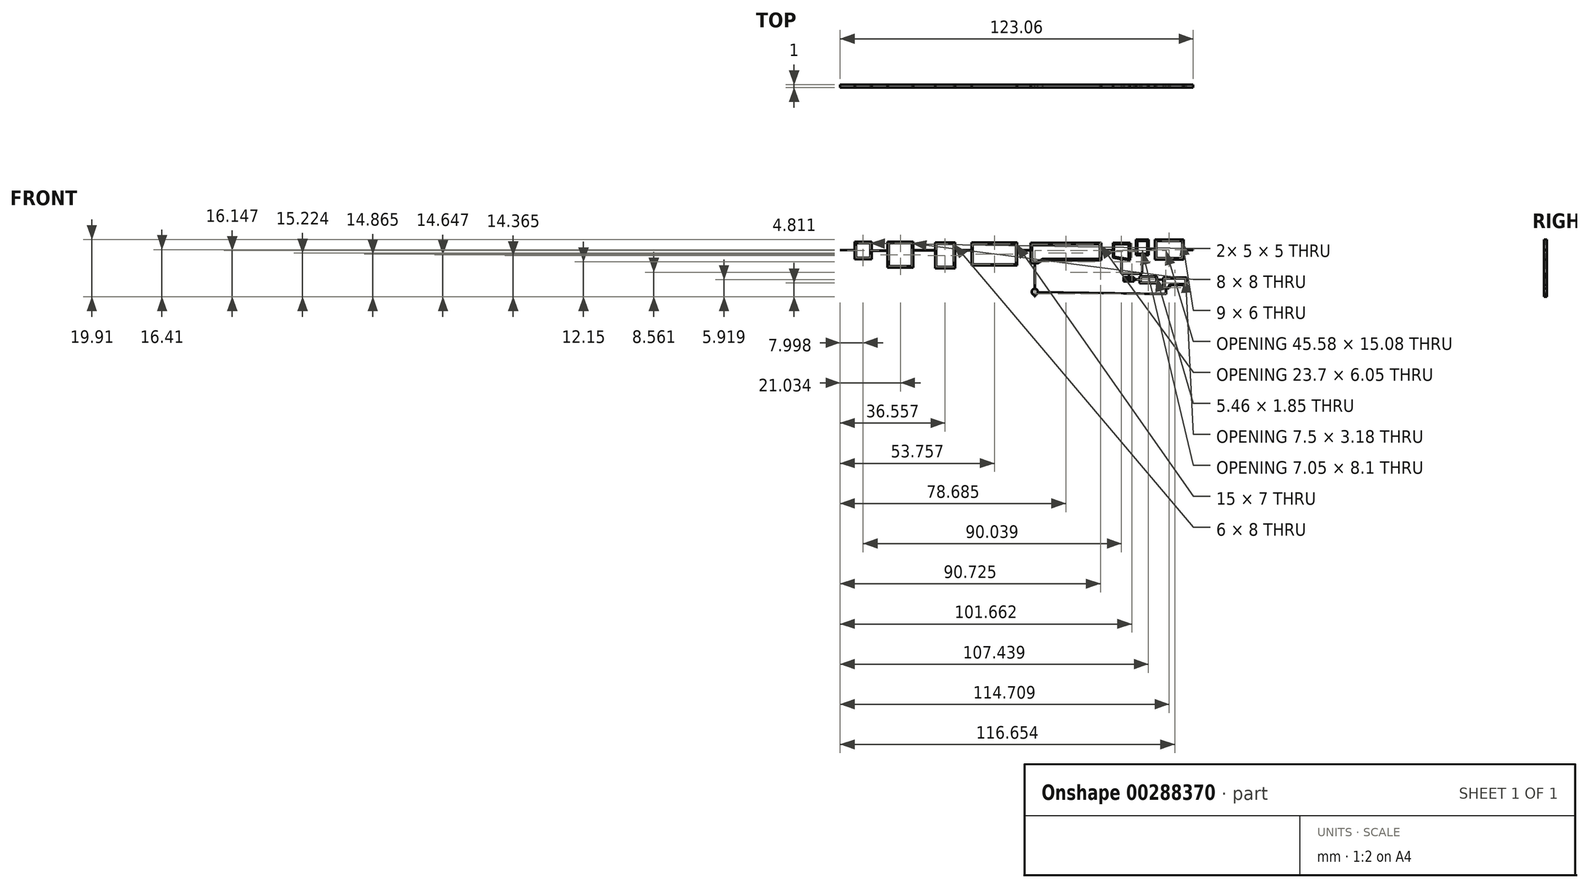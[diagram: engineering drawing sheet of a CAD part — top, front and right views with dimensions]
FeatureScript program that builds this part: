
annotation { "Feature Type Name" : "Feature", "Feature Type Description" : "" }
export const myFeature = defineFeature(function(context is Context, id is Id, definition is map)
    precondition{}
    {
        {
            var Q0;
            Q0=qCreatedBy(makeId("Front.planeOp"),FACE);
            var sketch = newSketch(context, id + "F0", { "sketchPlane" : qUnion([Q0])});
            skLineSegment(sketch, "E0.bottom", {"start": v(-63.05, 2.45) * mm, "end": v(-58.05, 2.45) * mm});
            skLineSegment(sketch, "E0.top", {"start": v(-63.05, -2.55) * mm, "end": v(-58.05, -2.55) * mm});
            skLineSegment(sketch, "E0.left", {"start": v(-63.05, 2.45) * mm, "end": v(-63.05, -2.55) * mm});
            skLineSegment(sketch, "E0.right", {"start": v(-58.05, 2.45) * mm, "end": v(-58.05, -2.55) * mm});
            skLineSegment(sketch, "E1.bottom", {"start": v(-51.52, 2.45) * mm, "end": v(-43.52, 2.45) * mm});
            skLineSegment(sketch, "E1.top", {"start": v(-51.52, -5.55) * mm, "end": v(-43.52, -5.55) * mm});
            skLineSegment(sketch, "E1.left", {"start": v(-51.52, 2.45) * mm, "end": v(-51.52, -5.55) * mm});
            skLineSegment(sketch, "E1.right", {"start": v(-43.52, 2.45) * mm, "end": v(-43.52, -5.55) * mm});
            skLineSegment(sketch, "E2.bottom", {"start": v(-35, -5.84) * mm, "end": v(-29, -5.84) * mm});
            skLineSegment(sketch, "E2.top", {"start": v(-35, 2.16) * mm, "end": v(-29, 2.16) * mm});
            skLineSegment(sketch, "E2.left", {"start": v(-35, -5.84) * mm, "end": v(-35, 2.16) * mm});
            skLineSegment(sketch, "E2.right", {"start": v(-29, -5.84) * mm, "end": v(-29, 2.16) * mm});
            skLineSegment(sketch, "E3.bottom", {"start": v(-22.3, 2.16) * mm, "end": v(-7.3, 2.16) * mm});
            skLineSegment(sketch, "E3.top", {"start": v(-22.3, -4.84) * mm, "end": v(-7.3, -4.84) * mm});
            skLineSegment(sketch, "E3.left", {"start": v(-22.3, 2.16) * mm, "end": v(-22.3, -4.84) * mm});
            skLineSegment(sketch, "E3.right", {"start": v(-7.3, 2.16) * mm, "end": v(-7.3, -4.84) * mm});
            skLineSegment(sketch, "E4", {"start": v(-1.72, -4) * mm, "end": v(0.28, -4) * mm});
            skLineSegment(sketch, "E5", {"start": v(0.28, -4) * mm, "end": v(1.99, -2.95) * mm});
            skLineSegment(sketch, "E6", {"start": v(1.99, -2.95) * mm, "end": v(21.99, -2.95) * mm});
            skPoint(sketch, "E7.endSnap0", {"position": v(-1.72, 1) * mm});
            skLineSegment(sketch, "E8", {"start": v(21.99, 2.05) * mm, "end": v(-1.72, 2.05) * mm});
            skPoint(sketch, "E9.startSnap0", {"position": v(21.99, -0.98) * mm});
            skLineSegment(sketch, "E10", {"start": v(26.99, 0.05) * mm, "end": v(26.99, 2.05) * mm});
            skLineSegment(sketch, "E11", {"start": v(26.99, 2.05) * mm, "end": v(31.99, 2.05) * mm});
            skLineSegment(sketch, "E12", {"start": v(31.99, 2.05) * mm, "end": v(31.99, -2.95) * mm});
            skLineSegment(sketch, "E13", {"start": v(31.99, -2.95) * mm, "end": v(26.99, -2.23) * mm});
            skLineSegment(sketch, "E14", {"start": v(26.99, -2.23) * mm, "end": v(26.99, 0.05) * mm});
            skLineSegment(sketch, "E15", {"start": v(34.99, 0) * mm, "end": v(34.99, 3.2) * mm});
            skLineSegment(sketch, "E16", {"start": v(34.99, 3.2) * mm, "end": v(38.49, 3.2) * mm});
            skLineSegment(sketch, "E17", {"start": v(38.49, 3.2) * mm, "end": v(38.49, -1.2) * mm});
            skLineSegment(sketch, "E18", {"start": v(38.49, -1.2) * mm, "end": v(34.99, -1.2) * mm});
            skLineSegment(sketch, "E19", {"start": v(34.99, -1.2) * mm, "end": v(34.99, 0) * mm});
            skLineSegment(sketch, "E20.bottom", {"start": v(41.66, 3.2) * mm, "end": v(50.66, 3.2) * mm});
            skLineSegment(sketch, "E20.top", {"start": v(41.66, -2.8) * mm, "end": v(50.66, -2.8) * mm});
            skLineSegment(sketch, "E20.left", {"start": v(41.66, 3.2) * mm, "end": v(41.66, -2.8) * mm});
            skLineSegment(sketch, "E20.right", {"start": v(50.66, 3.2) * mm, "end": v(50.66, -2.8) * mm});
            skLineSegment(sketch, "E21", {"start": v(36.74, -1.7) * mm, "end": v(36.74, -8.2) * mm});
            skLineSegment(sketch, "E22", {"start": v(29.49, -3.1) * mm, "end": v(29.49, -8.2) * mm});
            skLineSegment(sketch, "E23", {"start": v(36.74, -8.2) * mm, "end": v(29.49, -8.2) * mm});
            skLineSegment(sketch, "E24.MirrorCS", {"start": v(30.54, -9.65) * mm, "end": v(30.54, -10.54) * mm});
            skLineSegment(sketch, "E25.MirrorCS", {"start": v(46.35, -11.8) * mm, "end": v(45.88, -12.98) * mm});
            skLineSegment(sketch, "E26.MirrorCS", {"start": v(36.16, -9.35) * mm, "end": v(36.16, -11.2) * mm});
            skLineSegment(sketch, "E27.MirrorCS", {"start": v(33.66, -9.65) * mm, "end": v(33.66, -10.54) * mm});
            skLineSegment(sketch, "E28.MirrorCS", {"start": v(41.62, -9.35) * mm, "end": v(41.62, -11.2) * mm});
            skLineSegment(sketch, "E29.MirrorCS", {"start": v(45.88, -12.98) * mm, "end": v(44.35, -12.98) * mm});
            skLineSegment(sketch, "E30.MirrorCS", {"start": v(36.16, -9.35) * mm, "end": v(41.62, -9.35) * mm});
            skLineSegment(sketch, "E31.MirrorCS", {"start": v(36.16, -11.2) * mm, "end": v(41.62, -11.2) * mm});
            skLineSegment(sketch, "E32.MirrorCS", {"start": v(44.35, -12.98) * mm, "end": v(44.35, -9.8) * mm});
            skLineSegment(sketch, "E33.MirrorCS", {"start": v(51.85, -9.8) * mm, "end": v(51.85, -11.8) * mm});
            skLineSegment(sketch, "E34.MirrorCS", {"start": v(30.54, -9.65) * mm, "end": v(33.66, -9.65) * mm});
            skLineSegment(sketch, "E35.MirrorCS", {"start": v(44.35, -9.8) * mm, "end": v(51.85, -9.8) * mm});
            skLineSegment(sketch, "E36.MirrorCS", {"start": v(30.54, -10.54) * mm, "end": v(33.66, -10.54) * mm});
            skLineSegment(sketch, "E37.MirrorCS", {"start": v(51.85, -11.8) * mm, "end": v(46.35, -11.8) * mm});
            skLineSegment(sketch, "E38", {"start": v(-0.72, -4) * mm, "end": v(-0.72, -13.37) * mm});
            skPoint(sketch, "E39.endSnap0", {"position": v(45.12, -12.98) * mm});
            skLineSegment(sketch, "E40.0", {"start": v(-63.55, 2.95) * mm, "end": v(-57.55, 2.95) * mm});
            skLineSegment(sketch, "E40.1", {"start": v(-63.55, 2.95) * mm, "end": v(-63.55, -3.05) * mm});
            skLineSegment(sketch, "E40.2", {"start": v(-63.55, -3.05) * mm, "end": v(-57.55, -3.05) * mm});
            skLineSegment(sketch, "E40.3", {"start": v(-57.55, 2.95) * mm, "end": v(-57.55, -3.05) * mm});
            skLineSegment(sketch, "E41.0", {"start": v(-43.02, 2.95) * mm, "end": v(-43.02, -6.05) * mm});
            skLineSegment(sketch, "E41.1", {"start": v(-52.02, 2.95) * mm, "end": v(-43.02, 2.95) * mm});
            skLineSegment(sketch, "E41.2", {"start": v(-52.02, 2.95) * mm, "end": v(-52.02, -6.05) * mm});
            skLineSegment(sketch, "E41.3", {"start": v(-52.02, -6.05) * mm, "end": v(-43.02, -6.05) * mm});
            skLineSegment(sketch, "E42.0", {"start": v(-28.5, -6.34) * mm, "end": v(-28.5, 2.66) * mm});
            skLineSegment(sketch, "E42.1", {"start": v(-35.5, -6.34) * mm, "end": v(-28.5, -6.34) * mm});
            skLineSegment(sketch, "E42.2", {"start": v(-35.5, -6.34) * mm, "end": v(-35.5, 2.66) * mm});
            skLineSegment(sketch, "E42.3", {"start": v(-35.5, 2.66) * mm, "end": v(-28.5, 2.66) * mm});
            skLineSegment(sketch, "E43.0", {"start": v(-22.8, 2.66) * mm, "end": v(-6.8, 2.66) * mm});
            skLineSegment(sketch, "E43.1", {"start": v(-22.8, 2.66) * mm, "end": v(-22.8, -5.34) * mm});
            skLineSegment(sketch, "E43.2", {"start": v(-22.8, -5.34) * mm, "end": v(-6.8, -5.34) * mm});
            skLineSegment(sketch, "E43.3", {"start": v(-6.8, 2.66) * mm, "end": v(-6.8, -5.34) * mm});
            skLineSegment(sketch, "E44", {"start": v(21.99, 2.05) * mm, "end": v(21.99, -2.95) * mm});
            skLineSegment(sketch, "E45", {"start": v(-1.72, 2.05) * mm, "end": v(-1.72, -4) * mm});
            skLineSegment(sketch, "E46.0", {"start": v(22.49, 2.55) * mm, "end": v(22.49, -3.45) * mm});
            skLineSegment(sketch, "E46.1", {"start": v(-2.22, 2.55) * mm, "end": v(-2.22, -4.5) * mm});
            skLineSegment(sketch, "E46.2", {"start": v(-2.22, -4.5) * mm, "end": v(0.42, -4.5) * mm});
            skLineSegment(sketch, "E46.3", {"start": v(22.49, 2.55) * mm, "end": v(-2.22, 2.55) * mm});
            skLineSegment(sketch, "E46.4", {"start": v(0.42, -4.5) * mm, "end": v(2.13, -3.45) * mm});
            skLineSegment(sketch, "E46.5", {"start": v(2.13, -3.45) * mm, "end": v(22.49, -3.45) * mm});
            skLineSegment(sketch, "E47.0", {"start": v(36.64, -1.7) * mm, "end": v(36.64, -8.1) * mm});
            skLineSegment(sketch, "E47.1", {"start": v(36.64, -8.1) * mm, "end": v(29.59, -8.1) * mm});
            skLineSegment(sketch, "E47.2", {"start": v(29.59, -2.6) * mm, "end": v(29.59, -2.6) * mm});
            skLineSegment(sketch, "E48.0", {"start": v(32.49, -3.53) * mm, "end": v(26.49, -2.67) * mm});
            skLineSegment(sketch, "E48.1", {"start": v(32.49, 2.55) * mm, "end": v(32.49, -3.53) * mm});
            skLineSegment(sketch, "E48.2", {"start": v(26.49, -2.67) * mm, "end": v(26.49, 0.05) * mm});
            skLineSegment(sketch, "E48.3", {"start": v(26.49, 0.05) * mm, "end": v(26.49, 2.55) * mm});
            skLineSegment(sketch, "E48.4", {"start": v(26.49, 2.55) * mm, "end": v(32.49, 2.55) * mm});
            skLineSegment(sketch, "E49.trimOffspring", {"start": v(29.59, -3.11) * mm, "end": v(29.59, -8.1) * mm});
            skPoint(sketch, "E50.orphan", {"position": v(29.49, -2.6) * mm});
            skLineSegment(sketch, "E51.0", {"start": v(38.99, -1.7) * mm, "end": v(34.49, -1.7) * mm});
            skLineSegment(sketch, "E51.1", {"start": v(38.99, 3.7) * mm, "end": v(38.99, -1.7) * mm});
            skLineSegment(sketch, "E51.2", {"start": v(34.49, -1.7) * mm, "end": v(34.49, 0) * mm});
            skLineSegment(sketch, "E51.3", {"start": v(34.49, 0) * mm, "end": v(34.49, 3.7) * mm});
            skLineSegment(sketch, "E51.4", {"start": v(34.49, 3.7) * mm, "end": v(38.99, 3.7) * mm});
            skPoint(sketch, "E52.orphan", {"position": v(36.74, -1.2) * mm});
            skLineSegment(sketch, "E53.0", {"start": v(41.16, 3.7) * mm, "end": v(51.16, 3.7) * mm});
            skLineSegment(sketch, "E53.1", {"start": v(41.16, 3.7) * mm, "end": v(41.16, -3.3) * mm});
            skLineSegment(sketch, "E53.2", {"start": v(41.16, -3.3) * mm, "end": v(51.16, -3.3) * mm});
            skLineSegment(sketch, "E53.3", {"start": v(51.16, 3.7) * mm, "end": v(51.16, -3.3) * mm});
            skLineSegment(sketch, "E54.0", {"start": v(30.24, -9.35) * mm, "end": v(33.96, -9.35) * mm});
            skLineSegment(sketch, "E54.1", {"start": v(30.24, -9.35) * mm, "end": v(30.24, -10.84) * mm});
            skLineSegment(sketch, "E54.2", {"start": v(30.24, -10.84) * mm, "end": v(33.96, -10.84) * mm});
            skLineSegment(sketch, "E54.3", {"start": v(33.96, -9.35) * mm, "end": v(33.96, -10.84) * mm});
            skLineSegment(sketch, "E55.0", {"start": v(35.86, -9.05) * mm, "end": v(41.92, -9.05) * mm});
            skLineSegment(sketch, "E55.1", {"start": v(35.86, -9.05) * mm, "end": v(35.86, -11.5) * mm});
            skLineSegment(sketch, "E55.2", {"start": v(35.86, -11.5) * mm, "end": v(41.92, -11.5) * mm});
            skLineSegment(sketch, "E55.3", {"start": v(41.92, -9.05) * mm, "end": v(41.92, -11.5) * mm});
            skLineSegment(sketch, "E56.0", {"start": v(44.05, -13.28) * mm, "end": v(44.05, -9.5) * mm});
            skLineSegment(sketch, "E56.1", {"start": v(52.15, -9.5) * mm, "end": v(52.15, -12.1) * mm});
            skLineSegment(sketch, "E56.2", {"start": v(52.15, -12.1) * mm, "end": v(46.56, -12.1) * mm});
            skLineSegment(sketch, "E56.3", {"start": v(44.05, -9.5) * mm, "end": v(52.15, -9.5) * mm});
            skLineSegment(sketch, "E56.4", {"start": v(46.56, -12.1) * mm, "end": v(46.08, -13.28) * mm});
            skLineSegment(sketch, "E56.5", {"start": v(46.08, -13.28) * mm, "end": v(44.05, -13.28) * mm});
            skLineSegment(sketch, "E57", {"start": v(-57.55, -0.05) * mm, "end": v(-52.02, -0.05) * mm});
            skLineSegment(sketch, "E58", {"start": v(-43.02, 0) * mm, "end": v(-35.5, 0) * mm});
            skLineSegment(sketch, "E59", {"start": v(-28.5, 0) * mm, "end": v(-22.8, 0) * mm});
            skLineSegment(sketch, "E60", {"start": v(-6.8, 0) * mm, "end": v(-2.22, 0) * mm});
            skLineSegment(sketch, "E61", {"start": v(22.49, 0) * mm, "end": v(26.49, 0) * mm});
            skLineSegment(sketch, "E62", {"start": v(32.49, 0) * mm, "end": v(34.49, 0) * mm});
            skLineSegment(sketch, "E63", {"start": v(38.99, 0.46) * mm, "end": v(41.16, 0.46) * mm});
            skLineSegment(sketch, "E64", {"start": v(51.16, 0.2) * mm, "end": v(54.51, 0.2) * mm});
            skLineSegment(sketch, "E65", {"start": v(54.51, 0.2) * mm, "end": v(54.51, 0.1) * mm});
            skLineSegment(sketch, "E66", {"start": v(54.51, 0.1) * mm, "end": v(51.16, 0.1) * mm});
            skLineSegment(sketch, "E67", {"start": v(32.18, -8.2) * mm, "end": v(32.18, -9.35) * mm});
            skPoint(sketch, "E67.endSnap0", {"position": v(32.1, -9.35) * mm});
            skLineSegment(sketch, "E68", {"start": v(33.96, -10.1) * mm, "end": v(35.86, -10.1) * mm});
            skLineSegment(sketch, "E69", {"start": v(41.92, -10.17) * mm, "end": v(44.05, -10.17) * mm});
            skLineSegment(sketch, "E70", {"start": v(45.07, -13.28) * mm, "end": v(45.07, -15.28) * mm});
            skLineSegment(sketch, "E71", {"start": v(45.07, -15.28) * mm, "end": v(0.38, -14.6) * mm});
            skLineSegment(sketch, "E72.0", {"start": v(-0.62, -4) * mm, "end": v(-0.62, -13.38) * mm});
            skLineSegment(sketch, "E73", {"start": v(-0.62, -16.2) * mm, "end": v(-0.72, -16.2) * mm});
            skLineSegment(sketch, "E74.0", {"start": v(45.07, -15.18) * mm, "end": v(45.07, -15.18) * mm});
            skLineSegment(sketch, "E75.0", {"start": v(44.97, -13.28) * mm, "end": v(44.97, -15.18) * mm});
            skLineSegment(sketch, "E76.trimOffspring", {"start": v(44.97, -15.28) * mm, "end": v(44.97, -15.28) * mm});
            skLineSegment(sketch, "E77.trimOffspring", {"start": v(44.97, -15.18) * mm, "end": v(0.38, -14.5) * mm});
            skLineSegment(sketch, "E78.0", {"start": v(32.08, -8.2) * mm, "end": v(32.08, -9.35) * mm});
            skLineSegment(sketch, "E79.0", {"start": v(33.96, -10.2) * mm, "end": v(35.86, -10.2) * mm});
            skLineSegment(sketch, "E80.0", {"start": v(41.92, -10.27) * mm, "end": v(44.05, -10.27) * mm});
            skLineSegment(sketch, "E81.0", {"start": v(22.49, -0.1) * mm, "end": v(26.49, -0.1) * mm});
            skLineSegment(sketch, "E82.0", {"start": v(38.99, 0.36) * mm, "end": v(41.16, 0.36) * mm});
            skLineSegment(sketch, "E83.0", {"start": v(32.49, 0.1) * mm, "end": v(34.49, 0.1) * mm});
            skLineSegment(sketch, "E84.0", {"start": v(-6.8, -0.1) * mm, "end": v(-2.22, -0.1) * mm});
            skLineSegment(sketch, "E85.0", {"start": v(-28.5, -0.1) * mm, "end": v(-22.8, -0.1) * mm});
            skLineSegment(sketch, "E86.0", {"start": v(-43.02, -0.1) * mm, "end": v(-35.5, -0.1) * mm});
            skLineSegment(sketch, "E87.bottom", {"start": v(-63.55, 0) * mm, "end": v(-68.55, 0) * mm});
            skLineSegment(sketch, "E87.top", {"start": v(-63.55, 0.1) * mm, "end": v(-68.55, 0.1) * mm});
            skLineSegment(sketch, "E87.left", {"start": v(-63.55, 0) * mm, "end": v(-63.55, 0.1) * mm});
            skLineSegment(sketch, "E87.right", {"start": v(-68.55, 0) * mm, "end": v(-68.55, 0.1) * mm});
            skLineSegment(sketch, "E88.0", {"start": v(-57.55, -0.15) * mm, "end": v(-52.02, -0.15) * mm});
            skCircle(sketch, "E89", {"center": v(-0.72, -14.47) * mm, "radius": 1 * mm});
            skCircle(sketch, "E90.0", {"center": v(-0.72, -14.47) * mm, "radius": 1.1 * mm});
            skLineSegment(sketch, "E91.trimOffspring", {"start": v(-0.62, -15.47) * mm, "end": v(-0.62, -16.2) * mm});
            skLineSegment(sketch, "E92.trimOffspring", {"start": v(-0.72, -15.47) * mm, "end": v(-0.72, -16.2) * mm});
            skPoint(sketch, "E93.orphan", {"position": v(-0.62, -14.47) * mm});
            skSolve(sketch);
        }
        {
            var Q0;
            Q0 = qSketchRegion(id + "F0", true);
            extrude(context, id + "F1", {"entities" : qUnion([Q0]), "depth" : 1 * mm});
        }
    });
